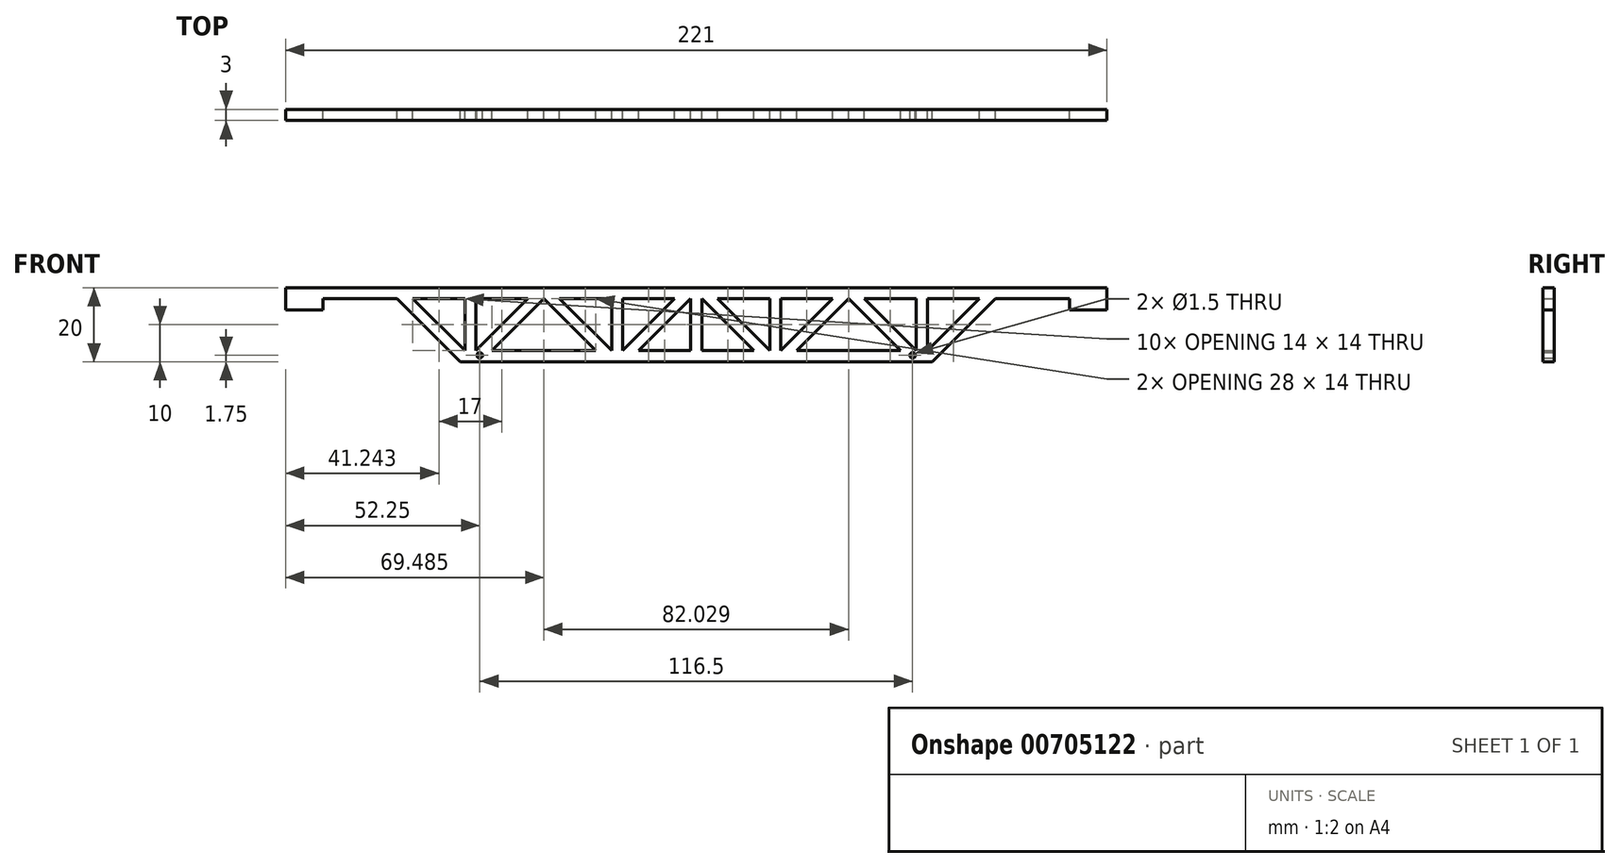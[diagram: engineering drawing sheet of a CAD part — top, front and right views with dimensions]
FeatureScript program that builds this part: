
annotation { "Feature Type Name" : "Feature", "Feature Type Description" : "" }
export const myFeature = defineFeature(function(context is Context, id is Id, definition is map)
    precondition{}
    {
        {
            var Q0;
            Q0=qCreatedBy(makeId("Front.planeOp"),FACE);
            var sketch = newSketch(context, id + "F0", { "sketchPlane" : qUnion([Q0])});
            skLineSegment(sketch, "E0.bottom", {"start": v(-100.5, 0) * mm, "end": v(-80.5, 0) * mm});
            skLineSegment(sketch, "E0.top", {"start": v(-110.5, 3) * mm, "end": v(0, 3) * mm});
            skLineSegment(sketch, "E0.left", {"start": v(-110.5, 0) * mm, "end": v(-110.5, 3) * mm});
            skLineSegment(sketch, "E0.right", {"start": v(0, 0) * mm, "end": v(0, 3) * mm});
            skLineSegment(sketch, "E1.top", {"start": v(-110.5, -3) * mm, "end": v(-100.5, -3) * mm});
            skLineSegment(sketch, "E1.left", {"start": v(-110.5, 0) * mm, "end": v(-110.5, -3) * mm});
            skLineSegment(sketch, "E1.right", {"start": v(-100.5, 0) * mm, "end": v(-100.5, -3) * mm});
            skLineSegment(sketch, "E2.bottom", {"start": v(0, -17) * mm, "end": v(-63.5, -17) * mm});
            skLineSegment(sketch, "E2.top", {"start": v(-1.53, -14) * mm, "end": v(-15.53, -14) * mm});
            skLineSegment(sketch, "E3", {"start": v(-80.5, 0) * mm, "end": v(-63.5, -17) * mm});
            skLineSegment(sketch, "E4", {"start": v(-76.26, 0) * mm, "end": v(-62.26, -14) * mm});
            skLineSegment(sketch, "E5.trimOffspring", {"start": v(-76.26, 0) * mm, "end": v(-62.26, 0) * mm});
            skLineSegment(sketch, "E6.top", {"start": v(-60.76, 0) * mm, "end": v(-59.26, 0) * mm});
            skLineSegment(sketch, "E6.left", {"start": v(-62.26, -14) * mm, "end": v(-62.26, 0) * mm});
            skLineSegment(sketch, "E6.right", {"start": v(-59.26, -14) * mm, "end": v(-59.26, 0) * mm});
            skLineSegment(sketch, "E7", {"start": v(-60.76, 0) * mm, "end": v(-60.76, -17) * mm, "construction": true});
            skLineSegment(sketch, "E8.MirrorCS", {"start": v(-45.26, 0) * mm, "end": v(-59.26, -14) * mm});
            skLineSegment(sketch, "E9.MirrorCS", {"start": v(-41.01, 0) * mm, "end": v(-55.01, -14) * mm});
            skPoint(sketch, "E10.orphan", {"position": v(-58.01, -17) * mm});
            skLineSegment(sketch, "E11", {"start": v(-41.01, 0) * mm, "end": v(-41.01, -14) * mm, "construction": true});
            skLineSegment(sketch, "E12.MirrorCS", {"start": v(-41.01, 0) * mm, "end": v(-27.01, -14) * mm});
            skLineSegment(sketch, "E13.MirrorCS", {"start": v(-36.77, 0) * mm, "end": v(-22.77, -14) * mm});
            skLineSegment(sketch, "E14.MirrorCS", {"start": v(-22.77, -14) * mm, "end": v(-22.77, 0) * mm});
            skLineSegment(sketch, "E15.MirrorCS", {"start": v(-19.77, -14) * mm, "end": v(-19.77, 0) * mm});
            skLineSegment(sketch, "E16.MirrorCS", {"start": v(-1.53, 0) * mm, "end": v(-15.53, -14) * mm});
            skLineSegment(sketch, "E17.MirrorCS", {"start": v(-5.77, 0) * mm, "end": v(-19.77, -14) * mm});
            skLineSegment(sketch, "E18.trimOffspring", {"start": v(-27.01, -14) * mm, "end": v(-55.01, -14) * mm});
            skPoint(sketch, "E19.orphan", {"position": v(-18.53, -17) * mm});
            skLineSegment(sketch, "E20", {"start": v(-1.53, 0) * mm, "end": v(-1.53, -14) * mm});
            skLineSegment(sketch, "E21.MirrorCS", {"start": v(62.26, 0) * mm, "end": v(59.26, 0) * mm});
            skLineSegment(sketch, "E22.MirrorCS", {"start": v(41.01, 0) * mm, "end": v(41.01, -14) * mm, "construction": true});
            skLineSegment(sketch, "E23.MirrorCS", {"start": v(60.76, 0) * mm, "end": v(60.76, -17) * mm, "construction": true});
            skPoint(sketch, "E24.MirrorP", {"position": v(18.53, -17) * mm});
            skLineSegment(sketch, "E25.MirrorCS", {"start": v(41.01, 0) * mm, "end": v(55.01, -14) * mm});
            skLineSegment(sketch, "E26.MirrorCS", {"start": v(41.01, 0) * mm, "end": v(27.01, -14) * mm});
            skLineSegment(sketch, "E27.MirrorCS", {"start": v(22.77, -14) * mm, "end": v(22.77, 0) * mm});
            skLineSegment(sketch, "E28.MirrorCS", {"start": v(19.77, -14) * mm, "end": v(19.77, 0) * mm});
            skLineSegment(sketch, "E29.MirrorCS", {"start": v(5.77, 0) * mm, "end": v(19.77, -14) * mm});
            skLineSegment(sketch, "E30.MirrorCS", {"start": v(1.53, 0) * mm, "end": v(1.53, -14) * mm});
            skLineSegment(sketch, "E31.MirrorCS", {"start": v(76.26, 0) * mm, "end": v(62.26, 0) * mm});
            skLineSegment(sketch, "E32.MirrorCS", {"start": v(76.26, 0) * mm, "end": v(62.26, -14) * mm});
            skLineSegment(sketch, "E33.MirrorCS", {"start": v(80.5, 0) * mm, "end": v(63.5, -17) * mm});
            skLineSegment(sketch, "E34.MirrorCS", {"start": v(1.53, -14) * mm, "end": v(15.53, -14) * mm});
            skLineSegment(sketch, "E35.MirrorCS", {"start": v(0, -17) * mm, "end": v(63.5, -17) * mm});
            skLineSegment(sketch, "E36.MirrorCS", {"start": v(100.5, 0) * mm, "end": v(100.5, -3) * mm});
            skLineSegment(sketch, "E37.MirrorCS", {"start": v(27.01, -14) * mm, "end": v(55.01, -14) * mm});
            skLineSegment(sketch, "E38.MirrorCS", {"start": v(110.5, 0) * mm, "end": v(110.5, -3) * mm});
            skLineSegment(sketch, "E39.MirrorCS", {"start": v(110.5, -3) * mm, "end": v(100.5, -3) * mm});
            skLineSegment(sketch, "E40.MirrorCS", {"start": v(1.53, 0) * mm, "end": v(15.53, -14) * mm});
            skLineSegment(sketch, "E41.MirrorCS", {"start": v(36.77, 0) * mm, "end": v(22.77, -14) * mm});
            skLineSegment(sketch, "E42.MirrorCS", {"start": v(110.5, 3) * mm, "end": v(0, 3) * mm});
            skLineSegment(sketch, "E43.MirrorCS", {"start": v(59.26, -14) * mm, "end": v(59.26, 0) * mm});
            skLineSegment(sketch, "E44.MirrorCS", {"start": v(110.5, 0) * mm, "end": v(110.5, 3) * mm});
            skPoint(sketch, "E45.MirrorP", {"position": v(58.01, -17) * mm});
            skLineSegment(sketch, "E46.MirrorCS", {"start": v(62.26, -14) * mm, "end": v(62.26, 0) * mm});
            skLineSegment(sketch, "E47.MirrorCS", {"start": v(100.5, 0) * mm, "end": v(80.5, 0) * mm});
            skLineSegment(sketch, "E48.MirrorCS", {"start": v(45.26, 0) * mm, "end": v(59.26, -14) * mm});
            skPoint(sketch, "E49.orphan", {"position": v(0, -14) * mm});
            skLineSegment(sketch, "E50.trimOffspring", {"start": v(-19.77, 0) * mm, "end": v(-5.77, 0) * mm});
            skLineSegment(sketch, "E51.trimOffspring", {"start": v(-36.77, 0) * mm, "end": v(-22.77, 0) * mm});
            skLineSegment(sketch, "E52.trimOffspring", {"start": v(19.77, 0) * mm, "end": v(5.77, 0) * mm});
            skLineSegment(sketch, "E53.trimOffspring", {"start": v(36.77, 0) * mm, "end": v(22.77, 0) * mm});
            skLineSegment(sketch, "E54.trimOffspring", {"start": v(59.26, 0) * mm, "end": v(45.26, 0) * mm});
            skPoint(sketch, "E55.orphan", {"position": v(41.01, -17) * mm});
            skPoint(sketch, "E56.orphan", {"position": v(-41.01, -17) * mm});
            skLineSegment(sketch, "E57.trimOffspring", {"start": v(-60.76, 0) * mm, "end": v(-45.26, 0) * mm});
            skCircle(sketch, "E58", {"center": v(-58.25, -15.25) * mm, "radius": 0.75 * mm});
            skLineSegment(sketch, "E59", {"start": v(0, -17) * mm, "end": v(0, -14) * mm, "construction": true});
            skCircle(sketch, "E60.MirrorC", {"center": v(58.25, -15.25) * mm, "radius": 0.75 * mm});
            skSolve(sketch);
        }
        {
            var Q0;
            Q0=makeQuery(id+"F0.imprint","IMPRINT",FACE,{"disambiguationData":[TD([[makeQuery(id+"F0.imprint","IMPRINT",EDGE,{"derivedFrom":sQuery(id+"F0.wireOp",EDGE,"E0.bottom")}),1.0]])]});
            extrude(context, id + "F1", {"entities" : qUnion([Q0]), "depth" : 3 * mm, "offsetDistance" : 25 * mm});
        }
    });
